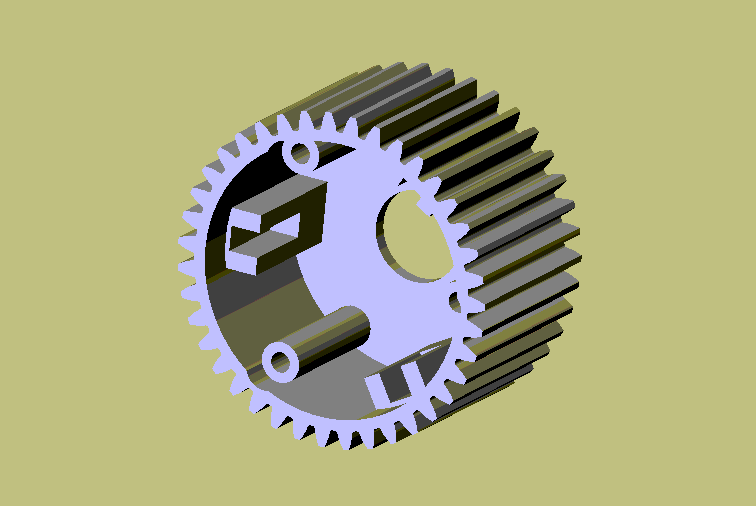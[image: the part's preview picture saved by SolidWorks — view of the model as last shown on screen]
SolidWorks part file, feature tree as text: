
SOLIDWORKS PART (.sldprt)
format: sldprt  version: not decoded by parser v0  size: 662,528 bytes
history: native  units: mm
features: sketch x30, cut_extrude x9, plane x4, extrude x3, material x1, fillet x1, pattern_circular x1 + 1 further entry (+9 scaffold rows collapsed)
feature tree (59):
  scaffold x9  (default folders/planes/origin — collapsed)
  material  "Matériau <non spécifié>"
  plane  "Plane1"
  plane  "Plane2"
  plane  "Plane3"
  "Famille de pièces"
  sketch  "Esquisse1"  dims[c1.D2=15.6mm c1.D1=42.0mm c2.D1=~4.615385deg]
  sketch  "Esquisse2"  dims[c1.D2=~15.286402mm c1.D1=37.0mm c2.D1=~5.385059deg]
  sketch  "Esquisse3"  dims[c1.D2=~14.972803mm c1.D1=33.0mm c2.D1=~5.988466deg]
  sketch  "Esquisse4"  dims[c1.D2=~14.659205mm c1.D1=30.0mm c2.D1=~6.323301deg]
  sketch  "Esquisse5"  dims[c1.D2=~15.866667mm c1.D1=46.0mm c2.D1=~3.858947deg]
  sketch  "Esquisse6"  dims[c1.D2=~16.133333mm c1.D1=50.0mm c2.D1=~3.024044deg]
  sketch  "Esquisse7"  dims[c1.D2=16.4mm c1.D1=54.0mm c2.D1=~2.120833deg]
  plane  "Plan1"  Offset=21mm
  sketch  "Esquisse8"  dims[c1.D2=15.6mm c1.D1=18.0mm c2.D1=~4.615385deg]
  sketch  "Esquisse9"  dims[c1.D2=~15.286402mm c1.D1=15.0mm c2.D1=~5.385059deg]
  sketch  "Esquisse10"  dims[c1.D2=~14.972803mm c1.D1=13.0mm c2.D1=~5.988466deg]
  sketch  "Esquisse11"  dims[c1.D2=~14.659205mm c1.D1=12.0mm c2.D1=~6.323301deg]
  sketch  "Esquisse12"  dims[c1.D2=~15.866667mm c1.D1=20.0mm c2.D1=~3.858947deg]
  sketch  "Esquisse13"  dims[c1.D2=~16.133333mm c1.D1=21.0mm c2.D1=~3.024044deg]
  sketch  "Esquisse14"  dims[c1.D2=16.4mm c1.D1=22.0mm c2.D1=~2.120833deg]
  sketch  "Esquisse15"  dims[c1.D2=14.6mm c1.D1=23.0mm c2.D1=~6.323301deg]
  sketch  "Esquisse16"  dims[c1.D2=14.6mm c1.D1=10.0mm c2.D1=~6.323301deg]
  sketch  "Esquisse17"  dims[D1=29.2mm]
  sketch  "Esquisse18"  dims[D1=29.2mm]
  fillet  "Congé1"  Radius=0.25mm
  pattern_circular  "Répétition circulaire1"  Count=39 Angle=360deg
  sketch  "Esquisse19"  dims[D1=27.0mm]
  cut_extrude  "Enlèv. mat.-Extru.1"  Depth=18mm
  sketch  "Esquisse20"  dims[D1=26.0mm]
  cut_extrude  "Enlèv. mat.-Extru.2"  Depth=2mm
  sketch  "Esquisse21"  dims[D1=12.0mm]
  extrude  "Boss.-Extru.1"  Depth=0.5mm
  sketch  "Esquisse22"  dims[D1=9.0mm]
  cut_extrude  "Enlèv. mat.-Extru.3"  [1 undecoded]
  sketch  "Esquisse23"  dims[D1=10.0mm D2=14.0mm]
  extrude  "Boss.-Extru.2"  Depth=13mm
  sketch  "Esquisse24"  dims[D1=2.5mm D2=3.0mm D3=10.0mm]
  cut_extrude  "Enlèv. mat.-Extru.4"  Depth=8mm
  sketch  "Esquisse25"  dims[c1.D3=4.0mm c1.D1=19.0mm c2.D1=30.0deg c2.D2=12.0mm]
  cut_extrude  "Enlèv. mat.-Extru.5"  [1 undecoded]
  sketch  "Esquisse26"
  extrude  "Boss.-Extru.3"  Depth=14mm
  sketch  "Esquisse27"  dims[D1=2.0mm D2=1.5mm]
  cut_extrude  "Enlèv. mat.-Extru.6"  Depth=6mm
  sketch  "Esquisse28"  dims[D1=2.0mm D2=2.0mm]
  cut_extrude  "Enlèv. mat.-Extru.7"  Depth=5mm
  sketch  "Esquisse29"
  cut_extrude  "Enlèv. mat.-Extru.8"  Depth=1mm
  sketch  "Esquisse30"
  cut_extrude  "Enlèv. mat.-Extru.9"  Depth=1mm
decode coverage: 39 of 44 modeling features carry decoded parameters; 1 rows unclassified (native names shown)
note: ~ marks probable driven/reference dimensions
note: 2 parameter values undecoded
note: suppression state not decoded; provenance and decode notes live in map.json
